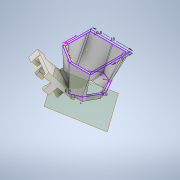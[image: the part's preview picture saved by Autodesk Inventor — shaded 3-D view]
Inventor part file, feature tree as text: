
AUTODESK INVENTOR PART (.ipt)
format: ipt  version: 2022 (Build 260153000, 153)  size: 540,160 bytes
history: native  units: in
note: dims shown in document units (in); Inventor stores cm internally (conversion verified against a paired STEP export)
features: sketch x10, plane x5, other x4, loft x4, extrude x1, split x1, move_body x1, revolve x1
ambient origin geometry x8: Origin, YZ Plane, XZ Plane, XY Plane, X Axis, Y Axis, Z Axis, Center Point
bodies: Solid1 (feature_tree)
feature tree (27):
  sketch  "Sketch1"  dims[d0=0.2441in d1=60.0deg]
  plane  "Work Plane1"
  plane  "Work Plane2"
  sketch  "Sketch2"  dims[d2=0.1063in d3=0.202in]
  other  "Repaired Geometry1"
  extrude  "Extrusion3"  TaperAngle=60.0deg  [1 undecoded]
  plane  "Work Plane5"
  sketch  "Sketch4"  dims[d8=0.0315in d11=0.1181in]
  plane  "Work Plane3"
  split  "Split3"
  sketch  "Sketch5"  dims[d14=0.0315in d15=0.0315in]
  plane  "Work Plane4"
  sketch  "Sketch6"  dims[d20=0.1181in d27=0.1181in d28=0.1181in d29=0.0in d30=0.0in]
  loft  "Loft3"
  other  "cam_holder_new_module"
  sketch  "Sketch7"  dims[d33=0.3937in]
  loft  "Loft5"
  move_body  "Move Body3"
  sketch  "Sketch9"  dims[d36=0.0315in]
  revolve  "Revolution1"  [1 undecoded]
  loft  "Loft9"
  loft  "Loft10"
  sketch  "Sketch11"  dims[d44=0.3543in d45=0.7087in d48=0.0315in d57=0.0in d58=90.0deg d59=0.0in d60=90.0deg d73=0.0933in d74=0.0315in d75=0.0984in d76=0.0591in d77=0.0591in d78=0.0in d79=90.0deg d80=0.0in d81=90.0deg d84=30.0deg d88=-0.2886in d89=-0.3125in d90=0.0394in d91=-0.1535in d100=0.3779in d105=0.0in d106=90.0deg d107=0.0in d108=90.0deg d109=0.0in d110=90.0deg d111=0.0in d112=90.0deg d101=0.0197in d102=0.0344in d103=0.0197in d104=0.0344in]
  sketch  "Sketch3"  dims[d4=0.1181in d7=0.0315in]
  sketch  "Sketch10"  dims[d40=0.6299in]
  other  "Composite1"
  other  "Srf1"
note: 2 required parameter values undecoded (feature->parameter linkage not recoverable at this tier; creation-order binding heuristic only, values carry confidence <= 0.55)